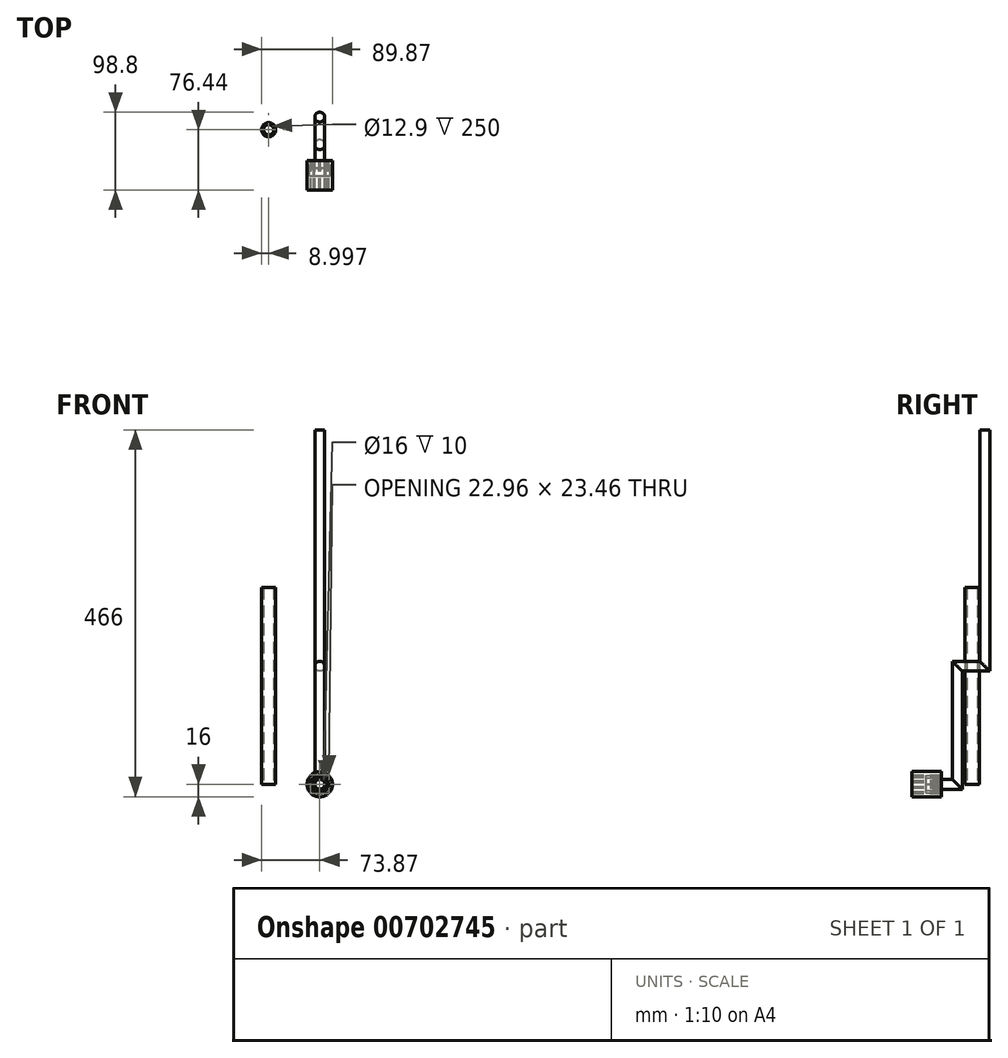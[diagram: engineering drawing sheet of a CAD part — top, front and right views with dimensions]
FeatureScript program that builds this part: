
annotation { "Feature Type Name" : "Feature", "Feature Type Description" : "" }
export const myFeature = defineFeature(function(context is Context, id is Id, definition is map)
    precondition{}
    {
        {
            var Q0;
            Q0=qCreatedBy(makeId("Right.planeOp"),FACE);
            var sketch = newSketch(context, id + "F0", { "sketchPlane" : qUnion([Q0])});
            skLineSegment(sketch, "E0.bottom", {"start": v(0, 0) * mm, "end": v(-37.5, 0) * mm});
            skLineSegment(sketch, "E0.top", {"start": v(0, 16) * mm, "end": v(-37.5, 16) * mm});
            skLineSegment(sketch, "E0.left", {"start": v(0, 0) * mm, "end": v(0, 16) * mm});
            skLineSegment(sketch, "E0.right", {"start": v(-37.5, 0) * mm, "end": v(-37.5, 16) * mm});
            skSolve(sketch);
        }
        {
            var Q0;
            Q0 = qSketchRegion(id + "F0", true);
            var Q1;
            Q1=sQuery(id+"F0.wireOp",EDGE,"E0.bottom");
            revolve(context, id + "F1", {"entities" : qUnion([Q0]), "axis" : qUnion([Q1]), "revolveType" : RevolveType.FULL});
        }
        {
            var Q0;
            Q0=qCreatedBy(makeId("Front.planeOp"),FACE);
            var sketch = newSketch(context, id + "F2", { "sketchPlane" : qUnion([Q0])});
            skCircle(sketch, "E1.cCircle", {"center": v(0, 0) * mm, "radius": 11.2 * mm, "construction": true});
            skLineSegment(sketch, "E1.0", {"start": v(10.83, -4.62) * mm, "end": v(6.05, -10.1) * mm});
            skLineSegment(sketch, "E1.1", {"start": v(6.05, -10.1) * mm, "end": v(-1.05, -11.73) * mm});
            skLineSegment(sketch, "E1.2", {"start": v(-1.05, -11.73) * mm, "end": v(-7.74, -8.87) * mm});
            skLineSegment(sketch, "E1.3", {"start": v(-7.74, -8.87) * mm, "end": v(-11.48, -2.63) * mm});
            skLineSegment(sketch, "E1.4", {"start": v(-11.48, -2.63) * mm, "end": v(-10.83, 4.62) * mm});
            skLineSegment(sketch, "E1.5", {"start": v(-10.83, 4.62) * mm, "end": v(-6.05, 10.1) * mm});
            skLineSegment(sketch, "E1.6", {"start": v(-6.05, 10.1) * mm, "end": v(1.05, 11.73) * mm});
            skLineSegment(sketch, "E1.7", {"start": v(1.05, 11.73) * mm, "end": v(7.74, 8.87) * mm});
            skLineSegment(sketch, "E1.8", {"start": v(7.74, 8.87) * mm, "end": v(11.48, 2.63) * mm});
            skLineSegment(sketch, "E1.9", {"start": v(11.48, 2.63) * mm, "end": v(10.83, -4.62) * mm});
            skPoint(sketch, "E1.0.midPoint", {"position": v(8.44, -7.36) * mm});
            skSolve(sketch);
        }
        {
            var Q0;
            Q0 = qSketchRegion(id + "F2", true);
            extrude(context, id + "F3", {"entities" : qUnion([Q0]), "operationType" : NewBodyOperationType.REMOVE, "depth" : 37.5 * mm, "offsetDistance" : 25 * mm});
        }
        {
            var Q0;
            Q0=qCreatedBy(makeId("Front.planeOp"),FACE);
            var sketch = newSketch(context, id + "F4", { "sketchPlane" : qUnion([Q0])});
            skCircle(sketch, "E2.cCircle", {"center": v(0, 0) * mm, "radius": 12.93 * mm, "construction": true});
            skLineSegment(sketch, "E2.0", {"start": v(6.32, -11.28) * mm, "end": v(-6.6, -11.1) * mm});
            skLineSegment(sketch, "E2.1", {"start": v(-6.6, -11.1) * mm, "end": v(-12.92, 0.17) * mm});
            skLineSegment(sketch, "E2.2", {"start": v(-12.92, 0.17) * mm, "end": v(-6.32, 11.28) * mm});
            skLineSegment(sketch, "E2.3", {"start": v(-6.32, 11.28) * mm, "end": v(6.6, 11.1) * mm});
            skLineSegment(sketch, "E2.4", {"start": v(6.6, 11.1) * mm, "end": v(12.92, -0.17) * mm});
            skLineSegment(sketch, "E2.5", {"start": v(12.92, -0.17) * mm, "end": v(6.32, -11.28) * mm});
            skSolve(sketch);
        }
        {
            var Q0;
            Q0 = qSketchRegion(id + "F4", true);
            extrude(context, id + "F5", {"entities" : qUnion([Q0]), "depth" : 20 * mm, "offsetDistance" : 25 * mm});
        }
        {
            var Q0;
            Q0=qCreatedBy(makeId("Front.planeOp"),FACE);
            var sketch = newSketch(context, id + "F6", { "sketchPlane" : qUnion([Q0])});
            skCircle(sketch, "E3", {"center": v(0, 0) * mm, "radius": 8 * mm});
            skSolve(sketch);
        }
        {
            var Q0;
            Q0 = qSketchRegion(id + "F6", true);
            extrude(context, id + "F7", {"entities" : qUnion([Q0]), "operationType" : NewBodyOperationType.REMOVE, "depth" : 30 * mm, "offsetDistance" : 25 * mm});
        }
        {
            var Q0;
            Q0=qCreatedBy(makeId("Front.planeOp"),FACE);
            var sketch = newSketch(context, id + "F8", { "sketchPlane" : qUnion([Q0])});
            skCircle(sketch, "E4", {"center": v(0, 0) * mm, "radius": 8 * mm});
            skSolve(sketch);
        }
        {
            var Q0;
            Q0 = qSketchRegion(id + "F8", true);
            extrude(context, id + "F9", {"entities" : qUnion([Q0]), "operationType" : NewBodyOperationType.ADD, "depth" : 10 * mm, "offsetDistance" : 25 * mm});
        }
        {
            var Q0;
            Q0=qCreatedBy(makeId("Front.planeOp"),FACE);
            var sketch = newSketch(context, id + "F10", { "sketchPlane" : qUnion([Q0])});
            skCircle(sketch, "E5.cCircle", {"center": v(0, 0) * mm, "radius": 6.35 * mm, "construction": true});
            skLineSegment(sketch, "E5.0", {"start": v(8.98, 0.26) * mm, "end": v(0.26, -8.98) * mm});
            skLineSegment(sketch, "E5.1", {"start": v(0.26, -8.98) * mm, "end": v(-8.98, -0.26) * mm});
            skLineSegment(sketch, "E5.2", {"start": v(-8.98, -0.26) * mm, "end": v(-0.26, 8.98) * mm});
            skLineSegment(sketch, "E5.3", {"start": v(-0.26, 8.98) * mm, "end": v(8.98, 0.26) * mm});
            skPoint(sketch, "E5.0.midPoint", {"position": v(4.62, -4.36) * mm});
            skSolve(sketch);
        }
        {
            var Q0;
            Q0 = qSketchRegion(id + "F10", true);
            extrude(context, id + "F11", {"entities" : qUnion([Q0]), "operationType" : NewBodyOperationType.REMOVE, "depth" : 12 * mm, "offsetDistance" : 25 * mm});
        }
        {
            var Q0;
            Q0=qCreatedBy(makeId("Front.planeOp"),FACE);
            var sketch = newSketch(context, id + "F12", { "sketchPlane" : qUnion([Q0])});
            skCircle(sketch, "E6", {"center": v(0, 0) * mm, "radius": 6.3 * mm});
            skSolve(sketch);
        }
        {
            var Q0;
            Q0 = qSketchRegion(id + "F12", true);
            extrude(context, id + "F13", {"entities" : qUnion([Q0]), "depth" : 10 * mm, "offsetDistance" : 25 * mm});
        }
        {
            var Q0;
            Q0=qCreatedBy(makeId("Right.planeOp"),FACE);
            var sketch = newSketch(context, id + "F14", { "sketchPlane" : qUnion([Q0])});
            skLineSegment(sketch, "E7", {"start": v(0, 0) * mm, "end": v(20, 0) * mm});
            skLineSegment(sketch, "E8", {"start": v(20, 0) * mm, "end": v(20, 150) * mm});
            skLineSegment(sketch, "E9", {"start": v(20, 150) * mm, "end": v(55, 150) * mm});
            skLineSegment(sketch, "E10", {"start": v(55, 150) * mm, "end": v(55, 450) * mm});
            skSolve(sketch);
        }
        {
            var Q0;
            Q0 = qSketchRegion(id + "F12", true);
            var Q1;
            Q1=sQuery(id+"F14.wireOp",EDGE,"E8");
            var Q2;
            Q2=sQuery(id+"F14.wireOp",EDGE,"E7");
            var Q3;
            Q3=sQuery(id+"F14.wireOp",EDGE,"E9");
            var Q4;
            Q4=sQuery(id+"F14.wireOp",EDGE,"E10");
            sweep(context, id + "F15", {"operationType" : NewBodyOperationType.ADD, "profiles" : qUnion([Q0]), "path" : qUnion([Q1, Q2, Q3, Q4])});
        }
        {
            var Q0;
            Q0=qCreatedBy(makeId("Top.planeOp"),FACE);
            var sketch = newSketch(context, id + "F16", { "sketchPlane" : qUnion([Q0])});
            skCircle(sketch, "E11", {"center": v(-64.87, 38.94) * mm, "radius": 9 * mm});
            skCircle(sketch, "E12", {"center": v(-64.87, 38.94) * mm, "radius": 6.45 * mm});
            skSolve(sketch);
        }
        {
            var Q0;
            Q0=makeQuery(id+"F16.imprint","IMPRINT",FACE,{"disambiguationData":[TD([[makeQuery(id+"F16.imprint","IMPRINT",EDGE,{"derivedFrom":sQuery(id+"F16.wireOp",EDGE,"E11")}),1.0]])]});
            extrude(context, id + "F17", {"entities" : qUnion([Q0]), "depth" : 250 * mm, "offsetDistance" : 25 * mm});
        }
    });
